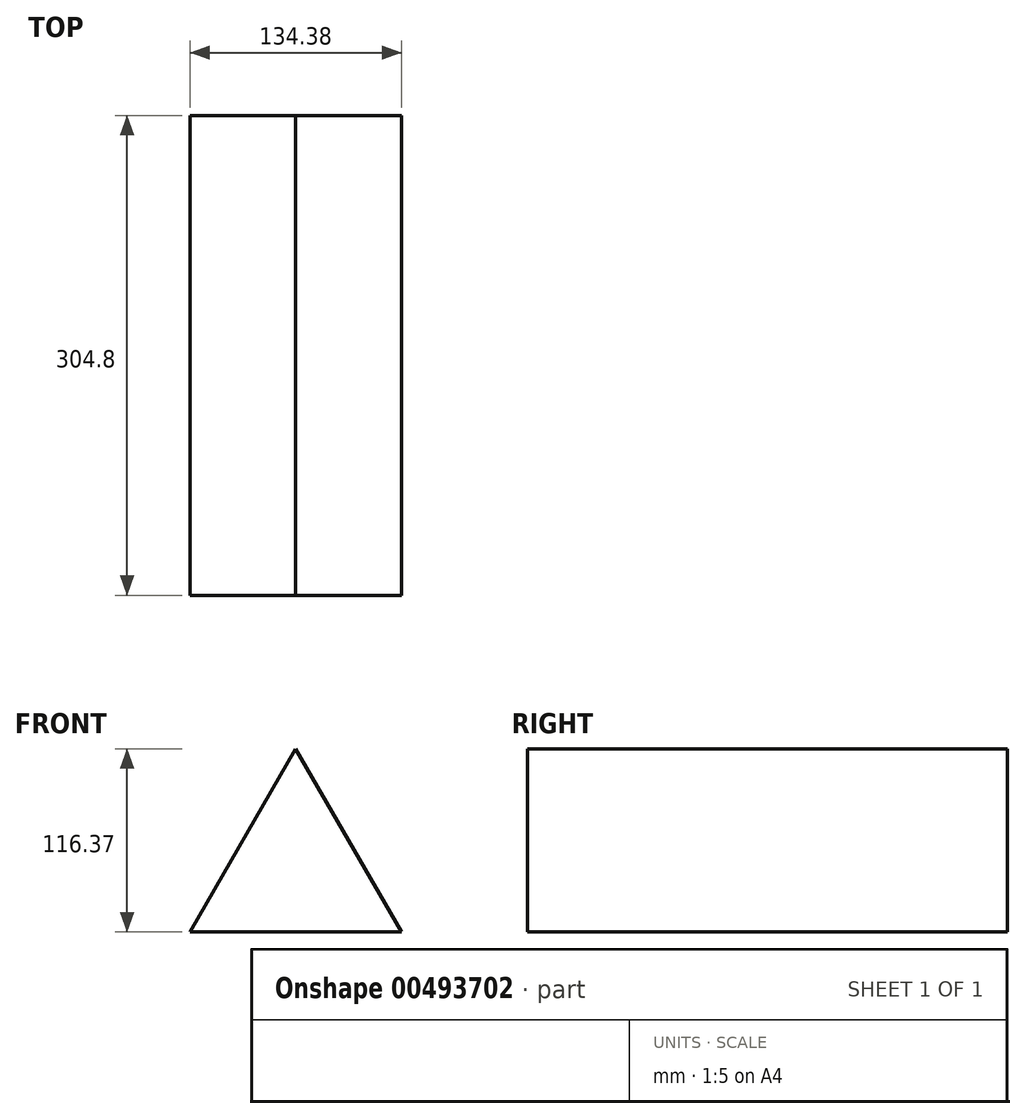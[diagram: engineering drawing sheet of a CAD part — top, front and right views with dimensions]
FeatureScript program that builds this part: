
annotation { "Feature Type Name" : "Feature", "Feature Type Description" : "" }
export const myFeature = defineFeature(function(context is Context, id is Id, definition is map)
    precondition{}
    {
        {
            var Q0;
            Q0=qCreatedBy(makeId("Front.planeOp"),FACE);
            var sketch = newSketch(context, id + "F0", { "sketchPlane" : qUnion([Q0])});
            skCircle(sketch, "E0.cCircle", {"center": v(0, 0) * mm, "radius": 77.58 * mm, "construction": true});
            skLineSegment(sketch, "E0.0", {"start": v(0, 77.58) * mm, "end": v(67.19, -38.8) * mm});
            skLineSegment(sketch, "E0.1", {"start": v(67.19, -38.8) * mm, "end": v(-67.19, -38.8) * mm});
            skLineSegment(sketch, "E0.2", {"start": v(-67.19, -38.8) * mm, "end": v(0, 77.58) * mm});
            skSolve(sketch);
        }
        {
            var Q0;
            Q0=makeQuery(id+"F0.imprint","IMPRINT",FACE,{"disambiguationData":[TD([[makeQuery(id+"F0.imprint","IMPRINT",EDGE,{"derivedFrom":sQuery(id+"F0.wireOp",EDGE,"E0.0")}),-1.0]])]});
            extrude(context, id + "F1", {"entities" : qUnion([Q0]), "depth" : 304.8 * mm});
        }
    });
